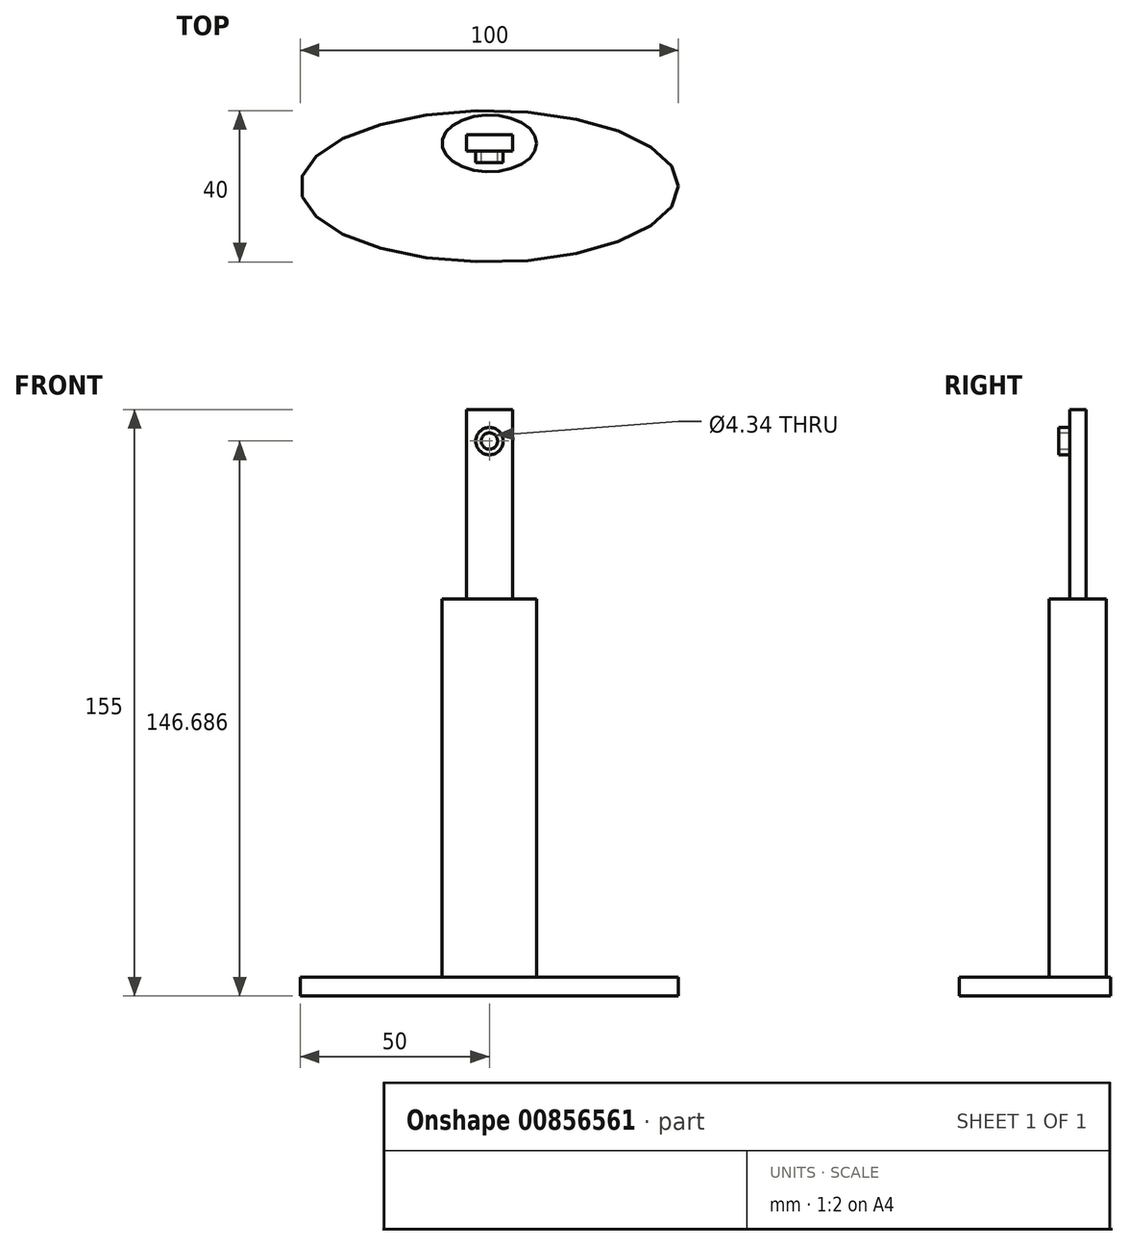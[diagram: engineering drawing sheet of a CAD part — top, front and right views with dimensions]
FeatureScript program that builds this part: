
annotation { "Feature Type Name" : "Feature", "Feature Type Description" : "" }
export const myFeature = defineFeature(function(context is Context, id is Id, definition is map)
    precondition{}
    {
        {
            var Q0;
            Q0=qCreatedBy(makeId("Top.planeOp"),FACE);
            var sketch = newSketch(context, id + "F0", { "sketchPlane" : qUnion([Q0])});
            skEllipse(sketch, "E0", {"center": v(0, 0) * mm, "majorRadius": 50 * mm, "minorRadius": 20 * mm, "majorAxis": v(1, 0)});
            skSolve(sketch);
        }
        {
            var Q0;
            Q0=makeQuery(id+"F0.imprint","IMPRINT",FACE,{"disambiguationData":[TD([[makeQuery(id+"F0.imprint","IMPRINT",EDGE,{"derivedFrom":sQuery(id+"F0.wireOp",EDGE,"E0")}),1.0]])]});
            extrude(context, id + "F1", {"entities" : qUnion([Q0]), "depth" : 5 * mm, "offsetDistance" : 25 * mm});
        }
        {
            var Q0;
            Q0=makeQuery(id+"F1.opExtrude","CAP_FACE",FACE,{"disambiguationData":[OSD([sQuery(id+"F0.wireOp",EDGE,"E0")])],"isStart":false});
            var sketch = newSketch(context, id + "F2", { "sketchPlane" : qUnion([Q0])});
            skSolve(sketch);
        }
        {
            var Q0;
            Q0=makeQuery(id+"F2.imprint","IMPRINT",FACE,{"disambiguationData":[TD([[makeQuery(id+"F2.imprint","IMPRINT",EDGE,{"derivedFrom":makeQuery(id+"F1.opExtrude","CAP_EDGE",EDGE,{"disambiguationData":[OSD([sQuery(id+"F0.wireOp",EDGE,"E0")])],"isStart":false})}),1.0]])]});
            var sketch = newSketch(context, id + "F3", { "sketchPlane" : qUnion([Q0])});
            skEllipse(sketch, "E1", {"center": v(0, 11.35) * mm, "majorRadius": 12.5 * mm, "minorRadius": 7.5 * mm, "majorAxis": v(1, 0)});
            skSolve(sketch);
        }
        {
            var Q0;
            Q0=makeQuery(id+"F3.imprint","IMPRINT",FACE,{"disambiguationData":[TD([[makeQuery(id+"F3.imprint","IMPRINT",EDGE,{"derivedFrom":sQuery(id+"F3.wireOp",EDGE,"E1")}),1.0]])]});
            extrude(context, id + "F4", {"entities" : qUnion([Q0]), "operationType" : NewBodyOperationType.ADD, "depth" : 100 * mm, "offsetDistance" : 25 * mm});
        }
        {
            var Q0;
            Q0=makeQuery(id+"F4.opExtrude","CAP_FACE",FACE,{"disambiguationData":[OSD([sQuery(id+"F3.wireOp",EDGE,"E1")])],"isStart":false});
            var sketch = newSketch(context, id + "F5", { "sketchPlane" : qUnion([Q0])});
            skLineSegment(sketch, "E2.bottom", {"start": v(-6.09, 13.62) * mm, "end": v(6.09, 13.62) * mm});
            skLineSegment(sketch, "E2.top", {"start": v(-6.09, 9.29) * mm, "end": v(6.09, 9.29) * mm});
            skLineSegment(sketch, "E2.left", {"start": v(-6.09, 13.62) * mm, "end": v(-6.09, 9.29) * mm});
            skLineSegment(sketch, "E2.right", {"start": v(6.09, 13.62) * mm, "end": v(6.09, 9.29) * mm});
            skSolve(sketch);
        }
        {
            var Q0;
            Q0=makeQuery(id+"F5.imprint","IMPRINT",FACE,{"disambiguationData":[TD([[makeQuery(id+"F5.imprint","IMPRINT",EDGE,{"derivedFrom":sQuery(id+"F5.wireOp",EDGE,"E2.bottom")}),-1.0]])]});
            extrude(context, id + "F6", {"entities" : qUnion([Q0]), "operationType" : NewBodyOperationType.ADD, "depth" : 50 * mm, "offsetDistance" : 25 * mm});
        }
        {
            var Q0;
            Q0=makeQuery(id+"F6.opExtrude","SWEPT_FACE",FACE,{"disambiguationData":[OSD([sQuery(id+"F5.wireOp",EDGE,"E2.top")])]});
            var sketch = newSketch(context, id + "F7", { "sketchPlane" : qUnion([Q0])});
            skCircle(sketch, "E3", {"center": v(0, 146.67) * mm, "radius": 3.61 * mm});
            skSolve(sketch);
        }
        {
            var Q0;
            Q0=makeQuery(id+"F7.imprint","IMPRINT",FACE,{"disambiguationData":[TD([[makeQuery(id+"F7.imprint","IMPRINT",EDGE,{"derivedFrom":sQuery(id+"F7.wireOp",EDGE,"E3")}),1.0]])]});
            var sketch = newSketch(context, id + "F8", { "sketchPlane" : qUnion([Q0])});
            skCircle(sketch, "E4", {"center": v(0, 146.69) * mm, "radius": 2.17 * mm});
            skSolve(sketch);
        }
        {
            var Q0;
            Q0=makeQuery(id+"F8.imprint","IMPRINT",FACE,{"disambiguationData":[TD([[makeQuery(id+"F8.imprint","IMPRINT",EDGE,{"derivedFrom":sQuery(id+"F8.wireOp",EDGE,"E4")}),-1.0]])]});
            extrude(context, id + "F9", {"entities" : qUnion([Q0]), "depth" : 3 * mm, "offsetDistance" : 25 * mm});
        }
    });
